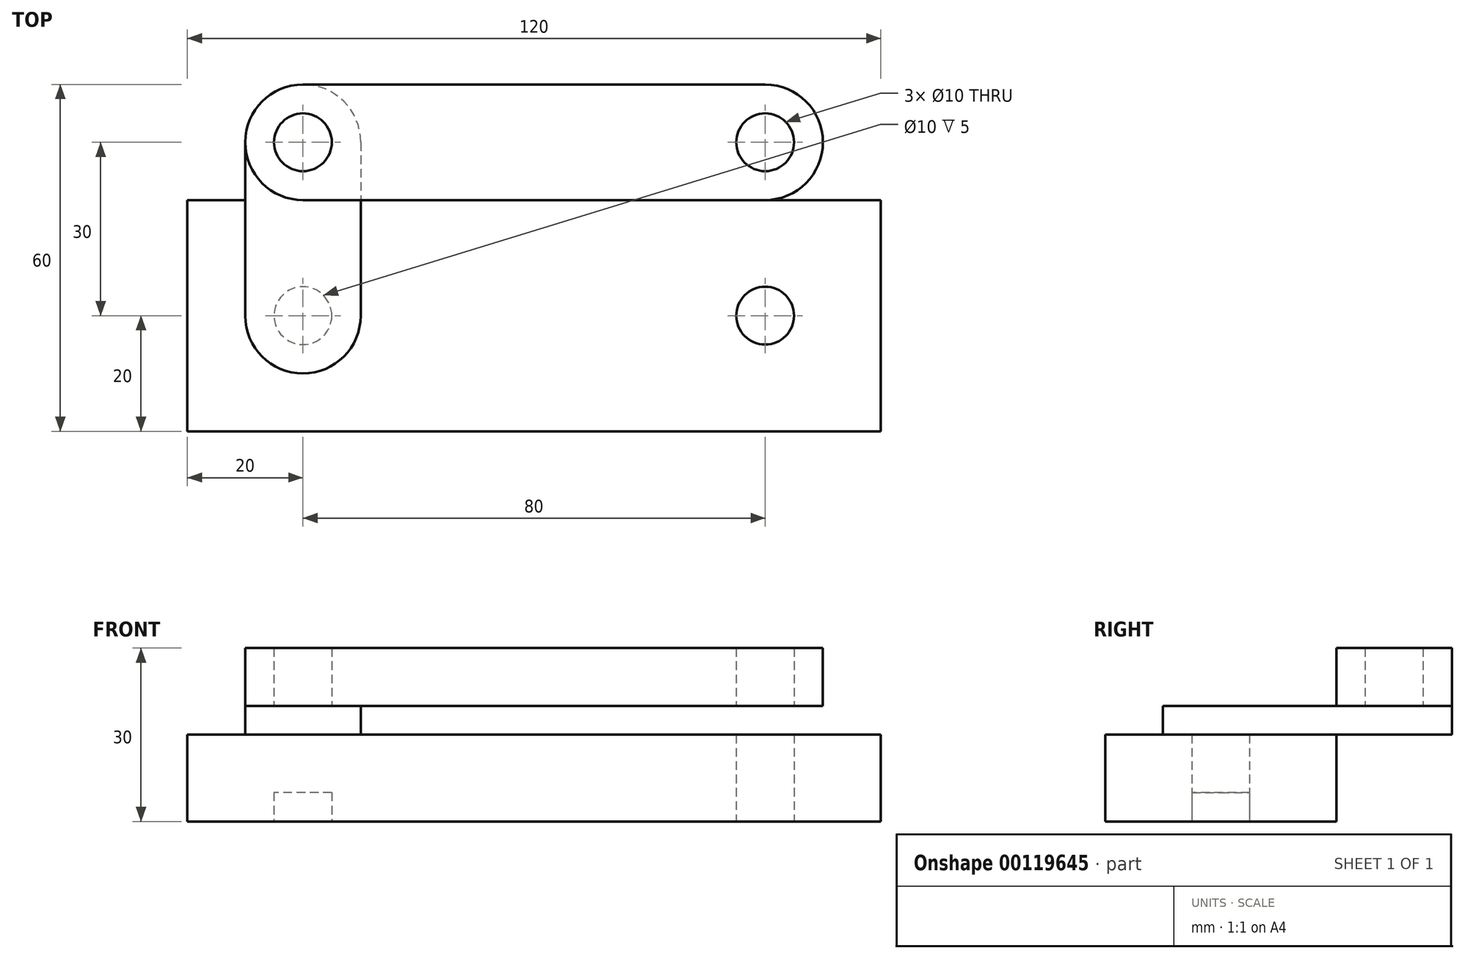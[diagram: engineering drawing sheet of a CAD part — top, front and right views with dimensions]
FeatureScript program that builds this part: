
annotation { "Feature Type Name" : "Feature", "Feature Type Description" : "" }
export const myFeature = defineFeature(function(context is Context, id is Id, definition is map)
    precondition{}
    {
        {
            var Q0;
            Q0=qCreatedBy(makeId("Top.planeOp"),FACE);
            var sketch = newSketch(context, id + "F0", { "sketchPlane" : qUnion([Q0])});
            skLineSegment(sketch, "E0.bottom", {"start": v(0, 0) * mm, "end": v(120, 0) * mm});
            skLineSegment(sketch, "E0.top", {"start": v(0, 40) * mm, "end": v(120, 40) * mm});
            skLineSegment(sketch, "E0.left", {"start": v(0, 0) * mm, "end": v(0, 40) * mm});
            skLineSegment(sketch, "E0.right", {"start": v(120, 0) * mm, "end": v(120, 40) * mm});
            skCircle(sketch, "E1", {"center": v(20, 20) * mm, "radius": 5 * mm});
            skPoint(sketch, "E1.centerSnap0", {"position": v(0, 20) * mm});
            skCircle(sketch, "E2", {"center": v(100, 20) * mm, "radius": 5 * mm});
            skSolve(sketch);
        }
        {
            var Q0;
            Q0=makeQuery(id+"F0.imprint","IMPRINT",FACE,{"disambiguationData":[TD([[makeQuery(id+"F0.imprint","IMPRINT",EDGE,{"derivedFrom":sQuery(id+"F0.wireOp",EDGE,"E0.bottom")}),1.0]])]});
            extrude(context, id + "F1", {"entities" : qUnion([Q0]), "depth" : 15 * mm});
        }
        {
            var Q0;
            Q0=makeQuery(id+"F1.opExtrude","CAP_FACE",FACE,{"disambiguationData":[OSD([sQuery(id+"F0.wireOp",EDGE,"E0.bottom"),sQuery(id+"F0.wireOp",EDGE,"E0.top"),sQuery(id+"F0.wireOp",EDGE,"E0.left"),sQuery(id+"F0.wireOp",EDGE,"E0.right"),sQuery(id+"F0.wireOp",EDGE,"E1"),sQuery(id+"F0.wireOp",EDGE,"E2")])],"isStart":false});
            var sketch = newSketch(context, id + "F2", { "sketchPlane" : qUnion([Q0])});
            skCircle(sketch, "E3", {"center": v(20, 20) * mm, "radius": 5 * mm});
            skCircle(sketch, "E4", {"center": v(20, 50) * mm, "radius": 5 * mm});
            skArc(sketch, "E5", {"start": v(30, 50) * mm, "mid": v(20, 60) * mm, "end": v(10, 50) * mm});
            skArc(sketch, "E6", {"start": v(10, 20) * mm, "mid": v(20, 10) * mm, "end": v(30, 20) * mm});
            skLineSegment(sketch, "E7", {"start": v(10, 50) * mm, "end": v(10, 20) * mm});
            skLineSegment(sketch, "E8", {"start": v(30, 50) * mm, "end": v(30, 20) * mm});
            skSolve(sketch);
        }
        {
            var Q0;
            Q0 = qSketchRegion(id + "F2", true);
            extrude(context, id + "F3", {"entities" : qUnion([Q0]), "depth" : 5 * mm});
        }
        {
            var Q0;
            Q0=makeQuery(id+"F2.imprint","IMPRINT",FACE,{"disambiguationData":[TD([[makeQuery(id+"F2.imprint","IMPRINT",EDGE,{"derivedFrom":sQuery(id+"F2.wireOp",EDGE,"E4")}),1.0]])]});
            extrude(context, id + "F4", {"entities" : qUnion([Q0]), "operationType" : NewBodyOperationType.ADD, "depth" : 15 * mm});
        }
        {
            var Q0;
            Q0=makeQuery(id+"F2.imprint","IMPRINT",FACE,{"disambiguationData":[TD([[makeQuery(id+"F2.imprint","IMPRINT",EDGE,{"derivedFrom":sQuery(id+"F2.wireOp",EDGE,"E3")}),1.0]])]});
            extrude(context, id + "F5", {"entities" : qUnion([Q0]), "operationType" : NewBodyOperationType.ADD, "depth" : 5 * mm, "hasSecondDirection" : true, "secondDirectionOppositeDirection" : true, "secondDirectionDepth" : 10 * mm});
        }
        {
            var Q0;
            {var subQ0=sQuery(id+"F2.wireOp",EDGE,"E3");Q0=makeQuery(id+"F5.boolean.opBoolean","MERGE",FACE,{"derivedFrom":[makeQuery(id+"F3.opExtrude","CAP_FACE",FACE,{"disambiguationData":[OSD([subQ0,sQuery(id+"F2.wireOp",EDGE,"E4"),sQuery(id+"F2.wireOp",EDGE,"E5"),sQuery(id+"F2.wireOp",EDGE,"E6"),sQuery(id+"F2.wireOp",EDGE,"E7"),sQuery(id+"F2.wireOp",EDGE,"E8")])],"isStart":false}),makeQuery(id+"F5.opExtrude","CAP_FACE",FACE,{"disambiguationData":[OSD([subQ0])],"isStart":false})]});}
            var sketch = newSketch(context, id + "F6", { "sketchPlane" : qUnion([Q0])});
            skCircle(sketch, "E9", {"center": v(20, 50) * mm, "radius": 5 * mm});
            skCircle(sketch, "E10", {"center": v(100, 50) * mm, "radius": 5 * mm});
            skArc(sketch, "E11", {"start": v(20, 60) * mm, "mid": v(10, 50) * mm, "end": v(20, 40) * mm});
            skArc(sketch, "E12", {"start": v(100, 40) * mm, "mid": v(110, 50) * mm, "end": v(100, 60) * mm});
            skLineSegment(sketch, "E13", {"start": v(20, 60) * mm, "end": v(100, 60) * mm});
            skLineSegment(sketch, "E14", {"start": v(20, 40) * mm, "end": v(100, 40) * mm});
            skSolve(sketch);
        }
        {
            var Q0;
            Q0=makeQuery(id+"F6.imprint","IMPRINT",FACE,{"disambiguationData":[TD([[makeQuery(id+"F6.imprint","IMPRINT",EDGE,{"derivedFrom":sQuery(id+"F6.wireOp",EDGE,"E10")}),-1.0]])]});
            var Q1;
            Q1=makeQuery(id+"F6.imprint","IMPRINT",FACE,{"disambiguationData":[TD([[makeQuery(id+"F6.imprint","IMPRINT",EDGE,{"derivedFrom":sQuery(id+"F6.wireOp",EDGE,"E9")}),-1.0]])]});
            extrude(context, id + "F7", {"entities" : qUnion([Q0, Q1]), "depth" : 10 * mm});
        }
    });
